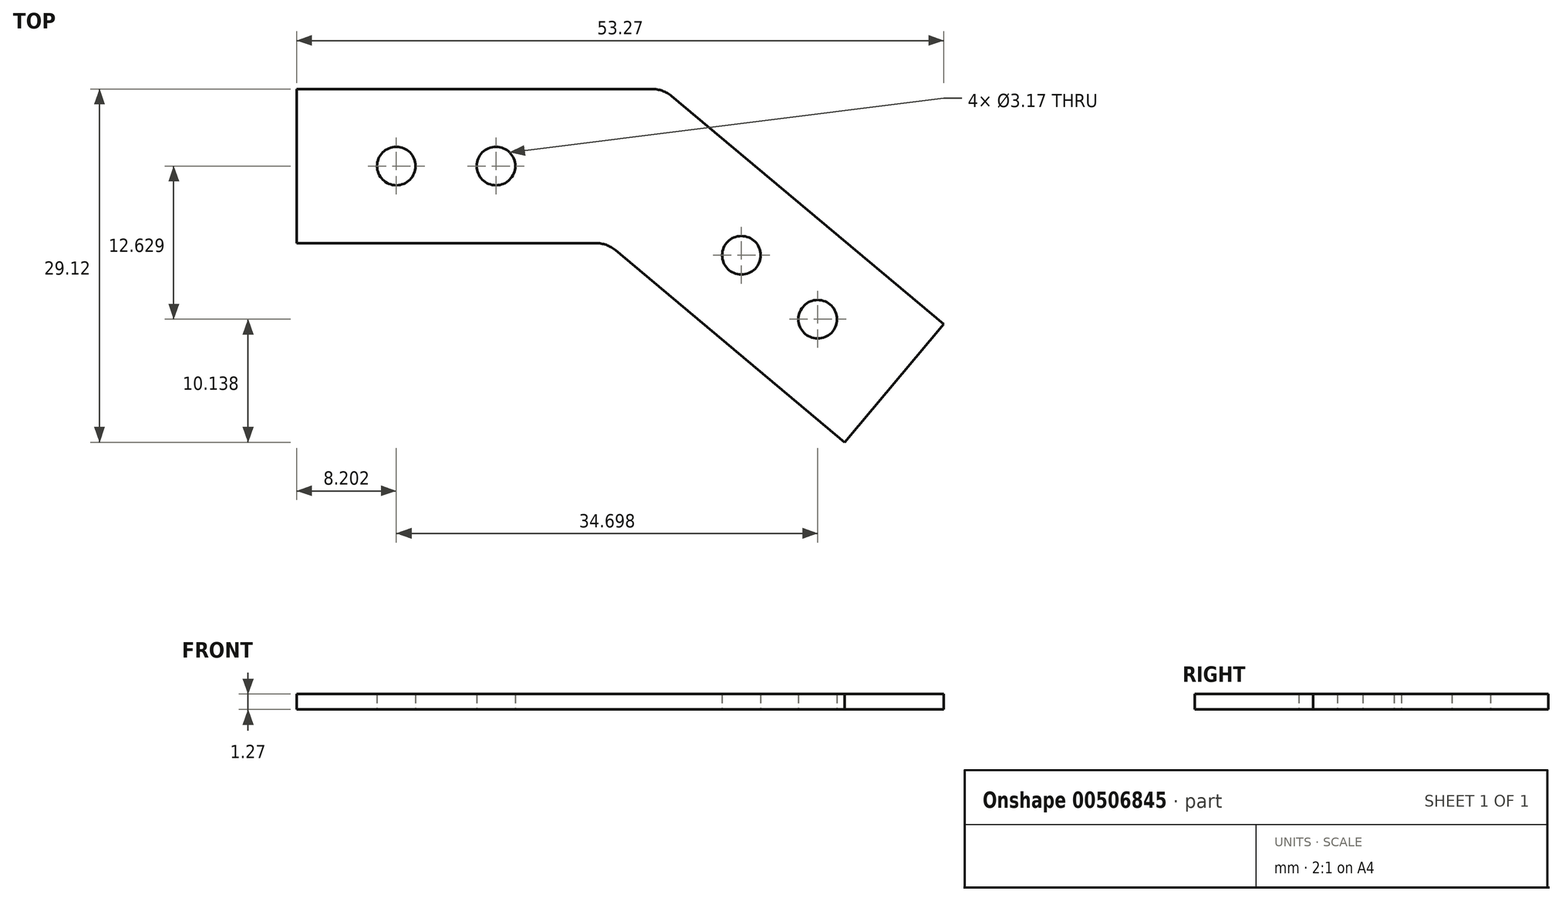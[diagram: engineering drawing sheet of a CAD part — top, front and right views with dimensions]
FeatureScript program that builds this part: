
annotation { "Feature Type Name" : "Feature", "Feature Type Description" : "" }
export const myFeature = defineFeature(function(context is Context, id is Id, definition is map)
    precondition{}
    {
        {
            var Q0;
            Q0=qCreatedBy(makeId("Top.planeOp"),FACE);
            var sketch = newSketch(context, id + "F0", { "sketchPlane" : qUnion([Q0])});
            skLineSegment(sketch, "E0", {"start": v(2.3, 29.12) * mm, "end": v(31.54, 29.12) * mm});
            skLineSegment(sketch, "E1", {"start": v(33.17, 28.52) * mm, "end": v(55.57, 9.73) * mm});
            skLineSegment(sketch, "E2", {"start": v(55.57, 9.73) * mm, "end": v(47.4, 0) * mm});
            skLineSegment(sketch, "E3", {"start": v(2.3, 29.12) * mm, "end": v(2.3, 16.42) * mm});
            skLineSegment(sketch, "E4", {"start": v(2.3, 16.42) * mm, "end": v(26.91, 16.42) * mm});
            skLineSegment(sketch, "E5", {"start": v(28.55, 15.82) * mm, "end": v(47.4, 0) * mm});
            skPoint(sketch, "E6.visualSharp", {"position": v(32.46, 29.12) * mm});
            skArc(sketch, "E6.filletArc", {"start": v(33.17, 28.52) * mm, "mid": v(32.4, 28.96) * mm, "end": v(31.54, 29.12) * mm});
            skPoint(sketch, "E7.visualSharp", {"position": v(27.84, 16.42) * mm});
            skArc(sketch, "E7.filletArc", {"start": v(28.55, 15.82) * mm, "mid": v(27.78, 16.26) * mm, "end": v(26.91, 16.42) * mm});
            skPoint(sketch, "E8", {"position": v(10.5, 22.77) * mm});
            skPoint(sketch, "E8.positionSnap0", {"position": v(2.3, 22.77) * mm});
            skPoint(sketch, "E9", {"position": v(18.7, 22.77) * mm});
            skPoint(sketch, "E10", {"position": v(45.2, 10.14) * mm});
            skPoint(sketch, "E11", {"position": v(38.92, 15.41) * mm});
            skSolve(sketch);
        }
        {
            var Q0;
            Q0=makeQuery(id+"F0.imprint","IMPRINT",FACE,{"disambiguationData":[TD([[makeQuery(id+"F0.imprint","IMPRINT",EDGE,{"derivedFrom":sQuery(id+"F0.wireOp",EDGE,"E0")}),-1.0]])]});
            extrude(context, id + "F1", {"entities" : qUnion([Q0]), "depth" : 1.27 * mm, "offsetDistance" : 25.4 * mm});
        }
        {
            var Q0;
            Q0=sQuery(id+"F0.wireOp",VERTEX,"E8");
            var Q1;
            Q1=sQuery(id+"F0.wireOp",VERTEX,"E9");
            var Q2;
            Q2=sQuery(id+"F0.wireOp",VERTEX,"E11");
            var Q3;
            Q3=sQuery(id+"F0.wireOp",VERTEX,"E10");
            var Q4;
            Q4=makeQuery(id+"F1.opExtrude","SWEPT_BODY",BODY,{"disambiguationData":[OSD([sQuery(id+"F0.wireOp",EDGE,"E0"),sQuery(id+"F0.wireOp",EDGE,"E1"),sQuery(id+"F0.wireOp",EDGE,"E2"),sQuery(id+"F0.wireOp",EDGE,"E3"),sQuery(id+"F0.wireOp",EDGE,"E4"),sQuery(id+"F0.wireOp",EDGE,"E5"),sQuery(id+"F0.wireOp",EDGE,"E6.filletArc"),sQuery(id+"F0.wireOp",EDGE,"E7.filletArc")])]});
            hole(context, id + "F2", {"style" : HoleStyle.SIMPLE, "endStyle" : HoleEndStyle.THROUGH, "oppositeDirection" : true, "holeDiameter" : 3.17 * mm, "majorDiameter" : 6.35 * mm, "isTappedThrough" : true, "tappedDepth" : 12.7 * mm, "tapClearance" : 3, "locations" : qUnion([Q0, Q1, Q2, Q3]), "scope" : qUnion([Q4])});
        }
    });
